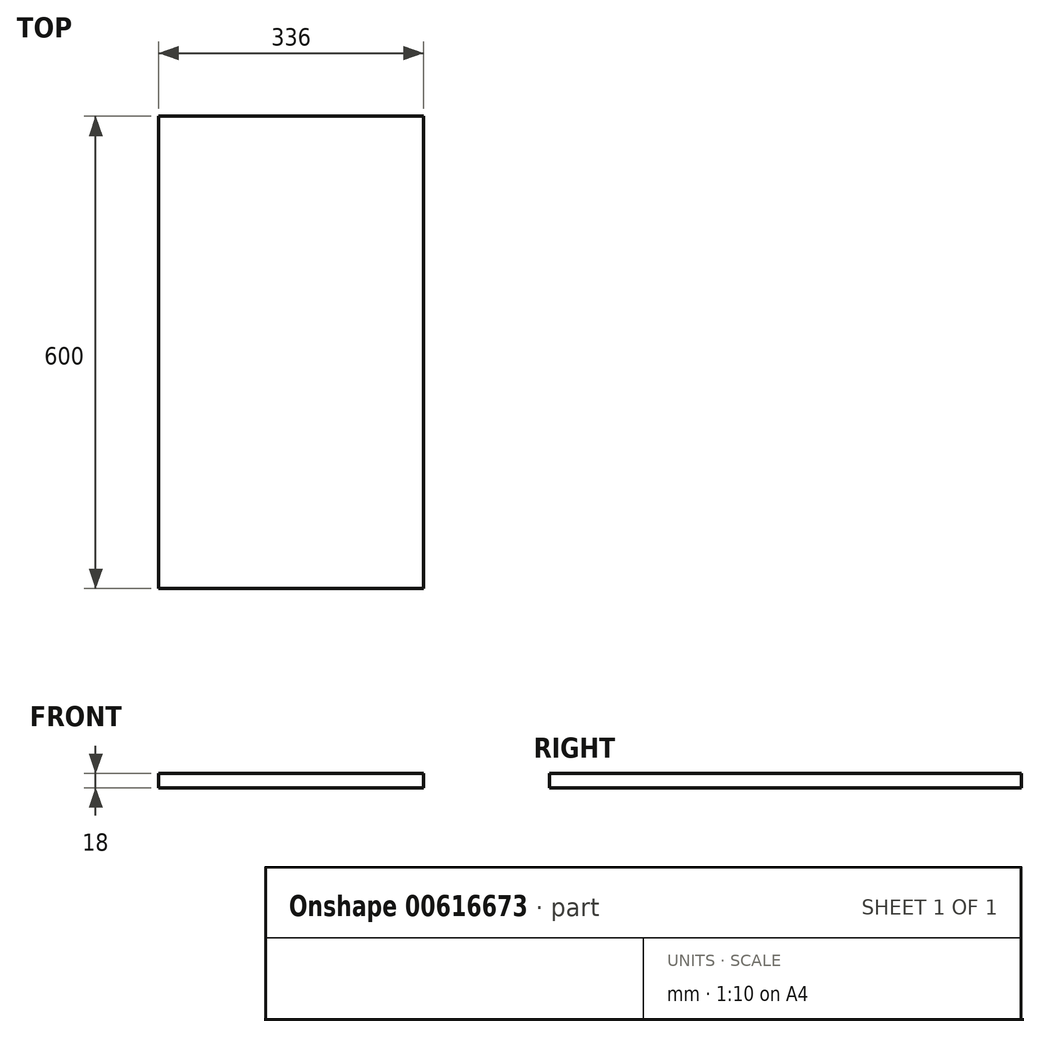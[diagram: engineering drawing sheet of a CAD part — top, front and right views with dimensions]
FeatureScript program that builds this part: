
annotation { "Feature Type Name" : "Feature", "Feature Type Description" : "" }
export const myFeature = defineFeature(function(context is Context, id is Id, definition is map)
    precondition{}
    {
        {
            var Q0;
            Q0=qCreatedBy(makeId("Top.planeOp"),FACE);
            var sketch = newSketch(context, id + "F0", { "sketchPlane" : qUnion([Q0])});
            skLineSegment(sketch, "E0.bottom", {"start": v(0, 0) * mm, "end": v(336, 0) * mm});
            skLineSegment(sketch, "E0.top", {"start": v(0, 600) * mm, "end": v(336, 600) * mm});
            skLineSegment(sketch, "E0.left", {"start": v(0, 0) * mm, "end": v(0, 600) * mm});
            skLineSegment(sketch, "E0.right", {"start": v(336, 0) * mm, "end": v(336, 600) * mm});
            skSolve(sketch);
        }
        {
            var Q0;
            Q0=makeQuery(id+"F0.imprint","IMPRINT",FACE,{"disambiguationData":[TD([[makeQuery(id+"F0.imprint","IMPRINT",EDGE,{"derivedFrom":sQuery(id+"F0.wireOp",EDGE,"E0.bottom")}),1.0]])]});
            extrude(context, id + "F1", {"entities" : qUnion([Q0]), "depth" : 18 * mm, "offsetDistance" : 25 * mm});
        }
    });
